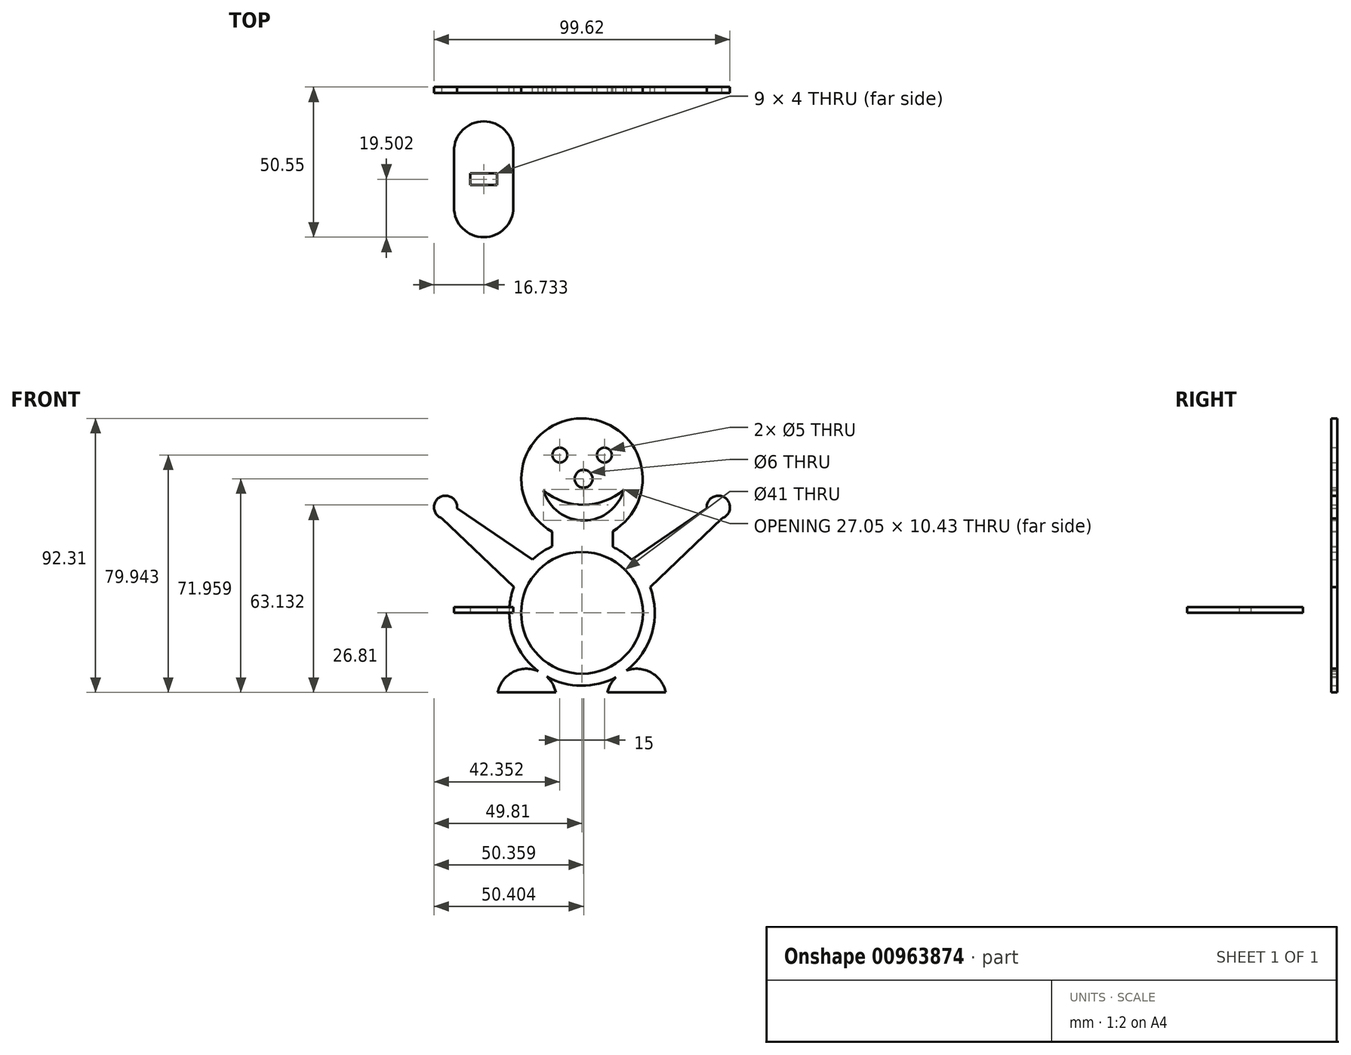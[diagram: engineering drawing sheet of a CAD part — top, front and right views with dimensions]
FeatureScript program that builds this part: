
annotation { "Feature Type Name" : "Feature", "Feature Type Description" : "" }
export const myFeature = defineFeature(function(context is Context, id is Id, definition is map)
    precondition{}
    {
        {
            var Q0;
            Q0=qCreatedBy(makeId("Front.planeOp"),FACE);
            var sketch = newSketch(context, id + "F0", { "sketchPlane" : qUnion([Q0])});
            skCircle(sketch, "E0", {"center": v(0, 0) * mm, "radius": 20.5 * mm});
            skArc(sketch, "E1.0", {"start": v(-10.05, 22.34) * mm, "mid": v(-13.55, 20.41) * mm, "end": v(-16.7, 17.94) * mm});
            skLineSegment(sketch, "E2", {"start": v(-10.05, 27.3) * mm, "end": v(-10.05, 22.34) * mm});
            skLineSegment(sketch, "E3", {"start": v(10.33, 27.48) * mm, "end": v(10.33, 22.21) * mm});
            skArc(sketch, "E4.trimOffspring", {"start": v(10.33, 27.48) * mm, "mid": v(-0.18, 65.5) * mm, "end": v(-10.05, 27.3) * mm});
            skPoint(sketch, "E5.center.orphan", {"position": v(0, 45.42) * mm});
            skArc(sketch, "E6", {"start": v(-8.6, -28.8) * mm, "mid": v(-9.44, -24.8) * mm, "end": v(-11.83, -21.46) * mm});
            skArc(sketch, "E7", {"start": v(28.4, -28.8) * mm, "mid": v(24.1, -20.6) * mm, "end": v(14.92, -19.43) * mm});
            skLineSegment(sketch, "E8", {"start": v(-28.6, -28.8) * mm, "end": v(-8.6, -28.8) * mm});
            skLineSegment(sketch, "E9.trimOffspring", {"start": v(8.4, -28.8) * mm, "end": v(28.4, -28.8) * mm});
            skCircle(sketch, "E10", {"center": v(-7.46, 53.13) * mm, "radius": 2.5 * mm});
            skCircle(sketch, "E11", {"center": v(7.54, 53.13) * mm, "radius": 2.5 * mm});
            skArc(sketch, "E12", {"start": v(-12.93, 41.22) * mm, "mid": v(0.72, 31.1) * mm, "end": v(14.12, 41.54) * mm});
            skArc(sketch, "E13", {"start": v(-12.93, 41.22) * mm, "mid": v(0.65, 36.39) * mm, "end": v(14.12, 41.54) * mm});
            skCircle(sketch, "E14", {"center": v(0.55, 45.15) * mm, "radius": 3 * mm});
            skArc(sketch, "E15.trimOffspring", {"start": v(-14.7, -19.6) * mm, "mid": v(-24.12, -20.47) * mm, "end": v(-28.6, -28.8) * mm});
            skArc(sketch, "E16.trimOffspring", {"start": v(11.35, -21.71) * mm, "mid": v(9.17, -24.96) * mm, "end": v(8.4, -28.8) * mm});
            skLineSegment(sketch, "E17", {"start": v(28.2, -26.8) * mm, "end": v(22.4, -26.8) * mm});
            skLineSegment(sketch, "E18.trimOffspring", {"start": v(-8.8, -26.8) * mm, "end": v(-14.6, -26.8) * mm});
            skLineSegment(sketch, "E19.top", {"start": v(-22.6, -28.8) * mm, "end": v(-14.6, -28.8) * mm});
            skLineSegment(sketch, "E20.top", {"start": v(14.4, -28.8) * mm, "end": v(22.4, -28.8) * mm});
            skLineSegment(sketch, "E20.left", {"start": v(14.4, -26.8) * mm, "end": v(14.4, -28.8) * mm});
            skLineSegment(sketch, "E20.right", {"start": v(22.4, -26.8) * mm, "end": v(22.4, -28.8) * mm});
            skLineSegment(sketch, "E21.trimOffspring", {"start": v(14.4, -26.8) * mm, "end": v(8.6, -26.8) * mm});
            skArc(sketch, "E22.trimOffspring", {"start": v(-11.83, -21.46) * mm, "mid": v(-0.27, -24.5) * mm, "end": v(11.35, -21.71) * mm});
            skArc(sketch, "E23.trimOffspring", {"start": v(14.92, -19.43) * mm, "mid": v(23.56, -6.73) * mm, "end": v(22.93, 8.62) * mm});
            skLineSegment(sketch, "E24.trimOffspring", {"start": v(-22.6, -26.8) * mm, "end": v(-28.4, -26.8) * mm});
            skLineSegment(sketch, "E25", {"start": v(14.4, -26.8) * mm, "end": v(22.4, -26.8) * mm});
            skLineSegment(sketch, "E26", {"start": v(-16.7, 17.94) * mm, "end": v(-42.01, 35.22) * mm});
            skArc(sketch, "E27", {"start": v(-42.01, 35.22) * mm, "mid": v(-48.05, 38.8) * mm, "end": v(-47.13, 31.84) * mm});
            skLineSegment(sketch, "E28", {"start": v(-47.13, 31.84) * mm, "end": v(-22.93, 8.62) * mm});
            skArc(sketch, "E29.trimOffspring", {"start": v(-22.97, 8.52) * mm, "mid": v(-23.5, -6.92) * mm, "end": v(-14.7, -19.6) * mm});
            skLineSegment(sketch, "E30.top", {"start": v(-22.6, -26.8) * mm, "end": v(-14.6, -26.8) * mm});
            skLineSegment(sketch, "E30.left", {"start": v(-22.6, -28.8) * mm, "end": v(-22.6, -26.8) * mm});
            skLineSegment(sketch, "E30.right", {"start": v(-14.6, -28.8) * mm, "end": v(-14.6, -26.8) * mm});
            skArc(sketch, "E31.MirrorCS", {"start": v(42.01, 35.22) * mm, "mid": v(48.05, 38.8) * mm, "end": v(47.13, 31.84) * mm});
            skLineSegment(sketch, "E32.MirrorCS", {"start": v(16.7, 17.94) * mm, "end": v(42.01, 35.22) * mm});
            skLineSegment(sketch, "E33.MirrorCS", {"start": v(47.13, 31.84) * mm, "end": v(22.93, 8.62) * mm});
            skArc(sketch, "E34.MirrorCS", {"start": v(-14.92, -19.43) * mm, "mid": v(-23.56, -6.73) * mm, "end": v(-22.93, 8.62) * mm});
            skLineSegment(sketch, "E35", {"start": v(-22.93, 8.62) * mm, "end": v(-22.93, 8.62) * mm});
            skArc(sketch, "E36.trimOffspring", {"start": v(-16.7, 17.94) * mm, "mid": v(-13.68, 20.32) * mm, "end": v(-10.33, 22.21) * mm});
            skArc(sketch, "E37.trimOffspring", {"start": v(16.7, 17.94) * mm, "mid": v(13.68, 20.32) * mm, "end": v(10.33, 22.21) * mm});
            skPoint(sketch, "E38.startSnap0", {"position": v(-0.18, 65.5) * mm});
            skSolve(sketch);
        }
        {
            var Q0;
            Q0=makeQuery(id+"F0.imprint","IMPRINT",FACE,{"disambiguationData":[TD([[makeQuery(id+"F0.imprint","IMPRINT",EDGE,{"derivedFrom":sQuery(id+"F0.wireOp",EDGE,"E0")}),-1.0]])]});
            var Q1;
            {var subQ0=sQuery(id+"F0.wireOp",EDGE,"E6");var subQ1=sQuery(id+"F0.wireOp",EDGE,"E1.0");var subQ2=makeQuery(id+"F0.imprint","INTERSECT",VERTEX,{"derivedFrom":[subQ1,subQ0]});Q1=makeQuery(id+"F0.imprint","IMPRINT",FACE,{"disambiguationData":[TD([[makeQuery(id+"F0.imprint","IMPRINT",EDGE,{"disambiguationData":[TD([[subQ2,1.0]])],"derivedFrom":subQ1}),-1.0]])]});}
            var Q2;
            Q2=makeQuery(id+"F0.imprint","IMPRINT",FACE,{"disambiguationData":[TD([[makeQuery(id+"F0.imprint","IMPRINT",EDGE,{"derivedFrom":sQuery(id+"F0.wireOp",EDGE,"E20.top")}),1.0]])]});
            var Q3;
            Q3=makeQuery(id+"F0.imprint","IMPRINT",FACE,{"disambiguationData":[TD([[makeQuery(id+"F0.imprint","IMPRINT",EDGE,{"derivedFrom":sQuery(id+"F0.wireOp",EDGE,"E19.top")}),1.0]])]});
            extrude(context, id + "F1", {"entities" : qUnion([Q0, Q1, Q2, Q3]), "depth" : 2 * mm, "offsetDistance" : 25 * mm});
        }
        {
            var Q0;
            Q0=qCreatedBy(makeId("Top.planeOp"),FACE);
            var sketch = newSketch(context, id + "F2", { "sketchPlane" : qUnion([Q0])});
            skLineSegment(sketch, "E39.left", {"start": v(-43.08, -21.55) * mm, "end": v(-43.08, -40.55) * mm});
            skLineSegment(sketch, "E39.right", {"start": v(-23.08, -21.55) * mm, "end": v(-23.08, -40.55) * mm});
            skArc(sketch, "E40", {"start": v(-43.08, -40.55) * mm, "mid": v(-33.08, -50.55) * mm, "end": v(-23.08, -40.55) * mm});
            skArc(sketch, "E41", {"start": v(-23.08, -21.55) * mm, "mid": v(-33.08, -11.55) * mm, "end": v(-43.08, -21.55) * mm});
            skLineSegment(sketch, "E42.bottom", {"start": v(-37.08, -29.55) * mm, "end": v(-29.08, -29.55) * mm});
            skLineSegment(sketch, "E42.top", {"start": v(-37.08, -32.55) * mm, "end": v(-29.08, -32.55) * mm});
            skLineSegment(sketch, "E42.left", {"start": v(-37.08, -29.55) * mm, "end": v(-37.08, -32.55) * mm});
            skLineSegment(sketch, "E42.right", {"start": v(-29.08, -29.55) * mm, "end": v(-29.08, -32.55) * mm});
            skLineSegment(sketch, "E43.0", {"start": v(-28.58, -29.05) * mm, "end": v(-28.58, -33.05) * mm});
            skLineSegment(sketch, "E43.1", {"start": v(-37.58, -29.05) * mm, "end": v(-28.58, -29.05) * mm});
            skLineSegment(sketch, "E43.2", {"start": v(-37.58, -29.05) * mm, "end": v(-37.58, -33.05) * mm});
            skLineSegment(sketch, "E43.3", {"start": v(-37.58, -33.05) * mm, "end": v(-28.58, -33.05) * mm});
            skSolve(sketch);
        }
        {
            var Q0;
            Q0=makeQuery(id+"F2.imprint","IMPRINT",FACE,{"disambiguationData":[TD([[makeQuery(id+"F2.imprint","IMPRINT",EDGE,{"derivedFrom":sQuery(id+"F2.wireOp",EDGE,"E39.left")}),1.0]])]});
            extrude(context, id + "F3", {"entities" : qUnion([Q0]), "depth" : 2 * mm, "offsetDistance" : 25 * mm});
        }
    });
